# Revit family: Smart_IR
name_source: partatom
category: Mechanical Equipment
units: mm (PartAtom-declared; Revit-internal decimal feet)

## family parameters
Always vertical = Yes
Classification = None
Cut with Voids When Loaded = No
Part Type = Normal
Room Calculation Point = No
Round Connector Dimension = Use Diameter
Shared = No
Work Plane-Based = No

## types (28) — shared parameters
00_20_Manufacturer = Blauberg
00_20_Name = Axial fan
Amperage = 0 A
Casing Material = Plastic, opaque, white
Description = For round channels
Height = 209 mm  [stored 0.685696 ft]
L = 56 mm  [stored 0.183727 ft]
Length = 56 mm  [stored 0.183727 ft]
Load Classification = HVAC
Maintenance zone material = <By Category>
Manufacturer = Blauberg
Number of Fase = 1
Power = 4 W
URL = https://blaubergventilatoren.de
Voltage = 230 V
Weight = 0.40 kg
Width = 155 mm  [stored 0.50853 ft]
a = 155 mm  [stored 0.50853 ft]
b = 209 mm  [stored 0.685696 ft]
c = 28 mm  [stored 0.0918635 ft]
e = 28 mm  [stored 0.0918635 ft]
zero-valued in all types: Default Elevation

## per-type parameters (varying)
| type | Apparent Load | Diameter | Dy | Frequency | Maximum Air Flow | Sound pressure level at 3 m distance | d | Панель |
| Smart 100 Brilliant red | 14 W | 100 mm  [stored 0.328084 ft] | 95 mm | 50 Hz | 106.0 m³/h | 31 dBA | 100 mm  [stored 0.328084 ft] | Panel : 100 Brilliant red |
| Smart 125 Madeira | 16 W | 125 mm  [stored 0.410105 ft] | 120 mm  [stored 0.393701 ft] | 0 Hz | 133.0 m³/h | 32 dBA | 125 mm  [stored 0.410105 ft] | Panel : 125 Madeira |
| Smart 100 Madeira | 14 W | 100 mm  [stored 0.328084 ft] | 95 mm | 50 Hz | 106.0 m³/h | 31 dBA | 100 mm  [stored 0.328084 ft] | Panel : 100 Madeira |
| Smart 125 Brilliant red | 16 W | 125 mm  [stored 0.410105 ft] | 120 mm  [stored 0.393701 ft] | 50 Hz | 133.0 m³/h | 32 dBA | 125 mm  [stored 0.410105 ft] | Panel : 125 Brilliant red |
| Smart 100 Savanna | 14 W | 100 mm  [stored 0.328084 ft] | 95 mm | 50 Hz | 106.0 m³/h | 31 dBA | 100 mm  [stored 0.328084 ft] | Panel : 100 Savanna |
| Smart 125 Savanna | 16 W | 125 mm  [stored 0.410105 ft] | 120 mm  [stored 0.393701 ft] | 50 Hz | 133.0 m³/h | 32 dBA | 125 mm  [stored 0.410105 ft] | Panel : 125 Savanna |
| Smart 100 Cosmos Black | 14 W | 100 mm  [stored 0.328084 ft] | 95 mm | 50 Hz | 106.0 m³/h | 31 dBA | 100 mm  [stored 0.328084 ft] | Panel : 100 Cosmos black |
| Smart 125 Cosmos Black | 16 W | 125 mm  [stored 0.410105 ft] | 120 mm  [stored 0.393701 ft] | 50 Hz | 133.0 m³/h | 32 dBA | 125 mm  [stored 0.410105 ft] | Panel : 125 Cosmos black |
| Smart 100 Royal Granit | 14 W | 100 mm  [stored 0.328084 ft] | 95 mm | 50 Hz | 106.0 m³/h | 31 dBA | 100 mm  [stored 0.328084 ft] | Panel : 100 Royal granit |
| Smart 125 Royal Granit | 16 W | 125 mm  [stored 0.410105 ft] | 120 mm  [stored 0.393701 ft] | 50 Hz | 133.0 m³/h | 32 dBA | 125 mm  [stored 0.410105 ft] | Panel : 125 Royal granit |
| Smart 100 Platinum | 14 W | 100 mm  [stored 0.328084 ft] | 95 mm | 50 Hz | 106.0 m³/h | 31 dBA | 100 mm  [stored 0.328084 ft] | Panel : 100 Platinum |
| Smart 125 Platinum | 16 W | 125 mm  [stored 0.410105 ft] | 120 mm  [stored 0.393701 ft] | 50 Hz | 133.0 m³/h | 32 dBA | 125 mm  [stored 0.410105 ft] | Panel : 125 Platinum |
| Smart 125 Volcano Gray | 16 W | 125 mm  [stored 0.410105 ft] | 120 mm  [stored 0.393701 ft] | 50 Hz | 133.0 m³/h | 32 dBA | 125 mm  [stored 0.410105 ft] | Panel : 125 Volcano Gray |
| Smart 100 Volcano Gray | 14 W | 100 mm  [stored 0.328084 ft] | 95 mm | 50 Hz | 106.0 m³/h | 31 dBA | 100 mm  [stored 0.328084 ft] | Panel : 100 Volcano Gray |
| Smart IR 100 Brilliant red | 14 W | 100 mm  [stored 0.328084 ft] | 95 mm | 50 Hz | 106.0 m³/h | 31 dBA | 100 mm  [stored 0.328084 ft] | Panel : 100 Brilliant red |
| Smart IR 100 Cosmos Black | 14 W | 100 mm  [stored 0.328084 ft] | 95 mm | 50 Hz | 106.0 m³/h | 31 dBA | 100 mm  [stored 0.328084 ft] | Panel : 100 Cosmos black |
| Smart IR 100 Madeira | 14 W | 100 mm  [stored 0.328084 ft] | 95 mm | 50 Hz | 106.0 m³/h | 31 dBA | 100 mm  [stored 0.328084 ft] | Panel : 100 Madeira |
| Smart IR 100 Platinum | 14 W | 100 mm  [stored 0.328084 ft] | 95 mm | 50 Hz | 106.0 m³/h | 31 dBA | 100 mm  [stored 0.328084 ft] | Panel : 100 Platinum |
| Smart IR 100 Royal Granit | 14 W | 100 mm  [stored 0.328084 ft] | 95 mm | 50 Hz | 106.0 m³/h | 31 dBA | 100 mm  [stored 0.328084 ft] | Panel : 100 Royal granit |
| Smart IR 100 Savanna | 14 W | 100 mm  [stored 0.328084 ft] | 95 mm | 50 Hz | 106.0 m³/h | 31 dBA | 100 mm  [stored 0.328084 ft] | Panel : 100 Savanna |
| Smart IR 100 Volcano Gray | 14 W | 100 mm  [stored 0.328084 ft] | 95 mm | 50 Hz | 106.0 m³/h | 31 dBA | 100 mm  [stored 0.328084 ft] | Panel : 100 Volcano Gray |
| Smart IR 125 Brilliant red | 16 W | 125 mm  [stored 0.410105 ft] | 120 mm  [stored 0.393701 ft] | 50 Hz | 133.0 m³/h | 32 dBA | 125 mm  [stored 0.410105 ft] | Panel : 125 Brilliant red |
| Smart IR 125 Cosmos Black | 16 W | 125 mm  [stored 0.410105 ft] | 120 mm  [stored 0.393701 ft] | 50 Hz | 133.0 m³/h | 32 dBA | 125 mm  [stored 0.410105 ft] | Panel : 125 Cosmos black |
| Smart IR 125 Madeira | 16 W | 125 mm  [stored 0.410105 ft] | 120 mm  [stored 0.393701 ft] | 0 Hz | 133.0 m³/h | 32 dBA | 125 mm  [stored 0.410105 ft] | Panel : 125 Madeira |
| Smart IR 125 Platinum | 16 W | 125 mm  [stored 0.410105 ft] | 120 mm  [stored 0.393701 ft] | 50 Hz | 133.0 m³/h | 32 dBA | 125 mm  [stored 0.410105 ft] | Panel : 125 Platinum |
| Smart IR125 Royal Granit | 16 W | 125 mm  [stored 0.410105 ft] | 120 mm  [stored 0.393701 ft] | 50 Hz | 133.0 m³/h | 32 dBA | 125 mm  [stored 0.410105 ft] | Panel : 125 Royal granit |
| Smart IR 125 Savanna | 16 W | 125 mm  [stored 0.410105 ft] | 120 mm  [stored 0.393701 ft] | 50 Hz | 133.0 m³/h | 32 dBA | 125 mm  [stored 0.410105 ft] | Panel : 125 Savanna |
| Smart IR 125 Volcano Gray | 16 W | 125 mm  [stored 0.410105 ft] | 120 mm  [stored 0.393701 ft] | 50 Hz | 133.0 m³/h | 32 dBA | 125 mm  [stored 0.410105 ft] | Panel : 125 Volcano Gray |

note: column(s) folded — value = type name in every type: 00_20_Type

note: [stored X ft] marks values corroborated as IEEE doubles in the binary element streams (Revit-internal decimal feet)
